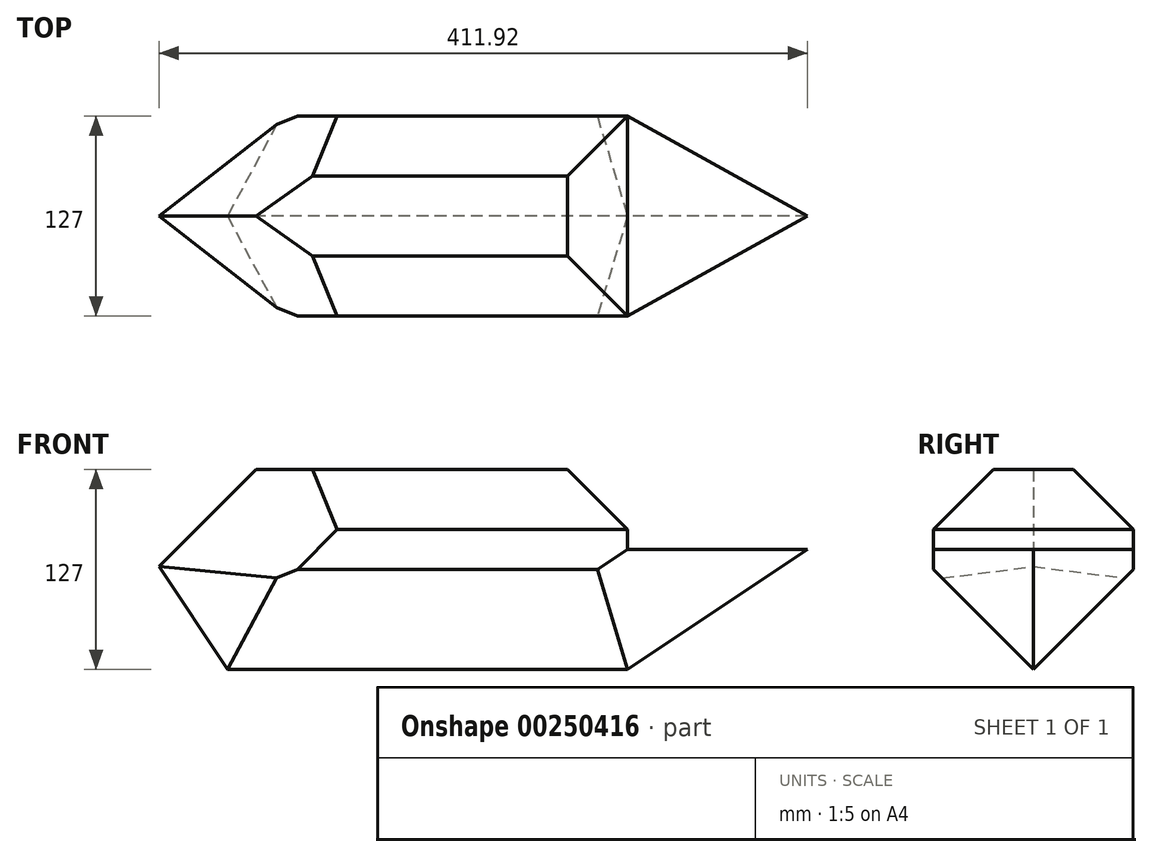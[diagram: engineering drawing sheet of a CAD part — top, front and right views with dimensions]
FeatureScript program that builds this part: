
annotation { "Feature Type Name" : "Feature", "Feature Type Description" : "" }
export const myFeature = defineFeature(function(context is Context, id is Id, definition is map)
    precondition{}
    {
        {
            var Q0;
            Q0=qCreatedBy(makeId("Front.planeOp"),FACE);
            var sketch = newSketch(context, id + "F0", { "sketchPlane" : qUnion([Q0])});
            skLineSegment(sketch, "E0.bottom", {"start": v(-160.61, 16.02) * mm, "end": v(93.39, 16.02) * mm});
            skLineSegment(sketch, "E0.top", {"start": v(-160.61, -60.18) * mm, "end": v(93.39, -60.18) * mm});
            skLineSegment(sketch, "E0.left", {"start": v(-160.61, 16.02) * mm, "end": v(-160.61, -60.18) * mm});
            skLineSegment(sketch, "E0.right", {"start": v(93.39, 16.02) * mm, "end": v(93.39, -60.18) * mm});
            skLineSegment(sketch, "E1", {"start": v(93.39, -60.18) * mm, "end": v(207.69, 16.02) * mm});
            skLineSegment(sketch, "E2", {"start": v(207.69, 16.02) * mm, "end": v(93.39, 16.02) * mm});
            skLineSegment(sketch, "E3", {"start": v(-160.61, -60.18) * mm, "end": v(-211.41, 16.02) * mm});
            skLineSegment(sketch, "E4", {"start": v(-211.41, 16.02) * mm, "end": v(-160.61, 16.02) * mm});
            skLineSegment(sketch, "E5", {"start": v(-211.41, 16.02) * mm, "end": v(-160.61, 66.82) * mm});
            skLineSegment(sketch, "E6", {"start": v(-160.61, 16.02) * mm, "end": v(-160.61, 66.82) * mm});
            skLineSegment(sketch, "E7", {"start": v(-160.61, 66.82) * mm, "end": v(93.39, 66.82) * mm});
            skLineSegment(sketch, "E8", {"start": v(93.39, 66.82) * mm, "end": v(93.39, 16.02) * mm});
            skLineSegment(sketch, "E9", {"start": v(93.39, 66.82) * mm, "end": v(207.69, 16.02) * mm});
            skSolve(sketch);
        }
        {
            var Q0;
            Q0=makeQuery(id+"F0.imprint","IMPRINT",FACE,{"disambiguationData":[TD([[makeQuery(id+"F0.imprint","IMPRINT",EDGE,{"derivedFrom":sQuery(id+"F0.wireOp",EDGE,"E0.bottom")}),-1.0]])]});
            extrude(context, id + "F1", {"entities" : qUnion([Q0]), "endBound" : BoundingType.SYMMETRIC, "depth" : 127 * mm});
        }
        {
            var Q0;
            Q0=makeQuery(id+"F1.opExtrude","CAP_EDGE",EDGE,{"disambiguationData":[OSD([sQuery(id+"F0.wireOp",EDGE,"E0.top")])],"isStart":false});
            var Q1;
            Q1=makeQuery(id+"F1.opExtrude","CAP_EDGE",EDGE,{"disambiguationData":[OSD([sQuery(id+"F0.wireOp",EDGE,"E0.top")])],"isStart":true});
            chamfer(context, id + "F2", {"entities" : qUnion([Q0, Q1]), "width" : 63.5 * mm, "tangentPropagation" : true});
        }
        {
            var Q0;
            Q0=makeQuery(id+"F0.imprint","IMPRINT",FACE,{"disambiguationData":[TD([[makeQuery(id+"F0.imprint","IMPRINT",EDGE,{"derivedFrom":sQuery(id+"F0.wireOp",EDGE,"E0.right")}),1.0]])]});
            extrude(context, id + "F3", {"entities" : qUnion([Q0]), "operationType" : NewBodyOperationType.ADD, "endBound" : BoundingType.SYMMETRIC, "depth" : 127 * mm});
        }
        {
            var Q0;
            Q0=makeQuery(id+"F3.opExtrude","CAP_EDGE",EDGE,{"disambiguationData":[OSD([sQuery(id+"F0.wireOp",EDGE,"E1")])],"isStart":false});
            chamfer(context, id + "F4", {"entities" : qUnion([Q0]), "width" : 63.5 * mm, "tangentPropagation" : true});
        }
        {
            var Q0;
            Q0=makeQuery(id+"F3.opExtrude","CAP_EDGE",EDGE,{"disambiguationData":[OSD([sQuery(id+"F0.wireOp",EDGE,"E1")])],"isStart":true});
            chamfer(context, id + "F5", {"entities" : qUnion([Q0]), "width" : 63.5 * mm, "tangentPropagation" : true});
        }
        {
            var Q0;
            Q0=makeQuery(id+"F0.imprint","IMPRINT",FACE,{"disambiguationData":[TD([[makeQuery(id+"F0.imprint","IMPRINT",EDGE,{"derivedFrom":sQuery(id+"F0.wireOp",EDGE,"E0.left")}),-1.0]])]});
            extrude(context, id + "F6", {"entities" : qUnion([Q0]), "operationType" : NewBodyOperationType.ADD, "endBound" : BoundingType.SYMMETRIC, "depth" : 127 * mm});
        }
        {
            var Q0;
            Q0=makeQuery(id+"F6.opExtrude","CAP_EDGE",EDGE,{"disambiguationData":[OSD([sQuery(id+"F0.wireOp",EDGE,"E3")])],"isStart":true});
            var Q1;
            Q1=makeQuery(id+"F6.opExtrude","CAP_EDGE",EDGE,{"disambiguationData":[OSD([sQuery(id+"F0.wireOp",EDGE,"E3")])],"isStart":false});
            chamfer(context, id + "F7", {"entities" : qUnion([Q0, Q1]), "width" : 63.5 * mm, "tangentPropagation" : true});
        }
        {
            var Q0;
            Q0=makeQuery(id+"F0.imprint","IMPRINT",FACE,{"disambiguationData":[TD([[makeQuery(id+"F0.imprint","IMPRINT",EDGE,{"derivedFrom":sQuery(id+"F0.wireOp",EDGE,"E0.bottom")}),1.0]])]});
            extrude(context, id + "F8", {"entities" : qUnion([Q0]), "operationType" : NewBodyOperationType.ADD, "endBound" : BoundingType.SYMMETRIC, "depth" : 127 * mm});
        }
        {
            var Q0;
            Q0=makeQuery(id+"F8.opExtrude","CAP_EDGE",EDGE,{"disambiguationData":[OSD([sQuery(id+"F0.wireOp",EDGE,"E7")])],"isStart":false});
            var Q1;
            Q1=makeQuery(id+"F8.opExtrude","CAP_EDGE",EDGE,{"disambiguationData":[OSD([sQuery(id+"F0.wireOp",EDGE,"E7")])],"isStart":true});
            var Q2;
            Q2=makeQuery(id+"F8.opExtrude","SWEPT_EDGE",EDGE,{"disambiguationData":[OSD([sQuery(id+"F0.wireOp",EDGE,"E7"),sQuery(id+"F0.wireOp",EDGE,"E8"),sQuery(id+"F0.wireOp",EDGE,"E9")])]});
            chamfer(context, id + "F9", {"entities" : qUnion([Q0, Q1, Q2]), "width" : 38.1 * mm, "tangentPropagation" : true});
        }
        {
            var Q0;
            Q0=makeQuery(id+"F0.imprint","IMPRINT",FACE,{"disambiguationData":[TD([[makeQuery(id+"F0.imprint","IMPRINT",EDGE,{"derivedFrom":sQuery(id+"F0.wireOp",EDGE,"E4")}),1.0]])]});
            extrude(context, id + "F10", {"entities" : qUnion([Q0]), "operationType" : NewBodyOperationType.ADD, "endBound" : BoundingType.SYMMETRIC, "depth" : 127 * mm});
        }
        {
            var Q0;
            Q0=makeQuery(id+"F10.opExtrude","CAP_EDGE",EDGE,{"disambiguationData":[OSD([sQuery(id+"F0.wireOp",EDGE,"E5")])],"isStart":false});
            var Q1;
            Q1=makeQuery(id+"F10.opExtrude","CAP_EDGE",EDGE,{"disambiguationData":[OSD([sQuery(id+"F0.wireOp",EDGE,"E5")])],"isStart":true});
            chamfer(context, id + "F11", {"entities" : qUnion([Q0, Q1]), "width" : 76.2 * mm, "tangentPropagation" : true});
        }
    });
